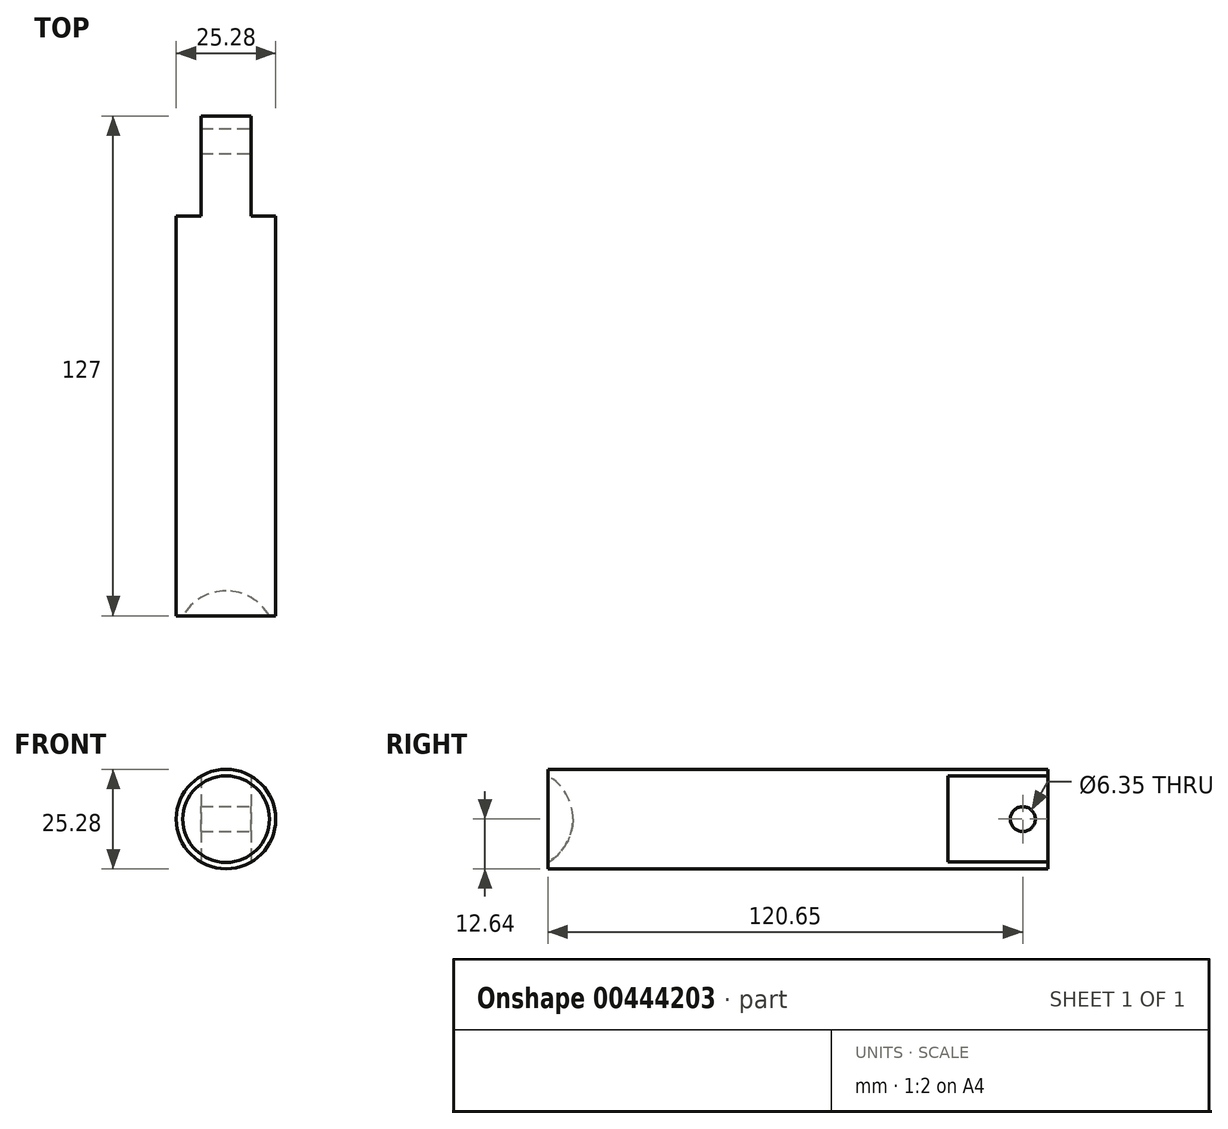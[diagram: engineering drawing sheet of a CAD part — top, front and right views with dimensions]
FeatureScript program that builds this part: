
annotation { "Feature Type Name" : "Feature", "Feature Type Description" : "" }
export const myFeature = defineFeature(function(context is Context, id is Id, definition is map)
    precondition{}
    {
        {
            var Q0;
            Q0=qCreatedBy(makeId("Right.planeOp"),FACE);
            var sketch = newSketch(context, id + "F0", { "sketchPlane" : qUnion([Q0])});
            skLineSegment(sketch, "E0.bottom", {"start": v(-63.5, 12.64) * mm, "end": v(63.5, 12.64) * mm});
            skLineSegment(sketch, "E0.left", {"start": v(-63.5, 12.64) * mm, "end": v(-63.5, 11) * mm});
            skLineSegment(sketch, "E0.right", {"start": v(63.5, 12.64) * mm, "end": v(63.5, 0) * mm});
            skArc(sketch, "E1", {"start": v(-57.15, 0) * mm, "mid": v(-58.85, 6.35) * mm, "end": v(-63.5, 11) * mm});
            skLineSegment(sketch, "E2", {"start": v(-57.15, 0) * mm, "end": v(63.5, 0) * mm});
            skPoint(sketch, "E3.orphan", {"position": v(63.5, -12.64) * mm});
            skLineSegment(sketch, "E4", {"start": v(-86.42, 0) * mm, "end": v(94.67, 0) * mm});
            skSolve(sketch);
        }
        {
            var Q0;
            Q0 = qSketchRegion(id + "F0", true);
            var Q1;
            Q1=sQuery(id+"F0.wireOp",EDGE,"E4");
            revolve(context, id + "F1", {"entities" : qUnion([Q0]), "axis" : qUnion([Q1]), "revolveType" : RevolveType.FULL});
        }
        {
            var Q0;
            Q0=makeQuery(id+"F1.opRevolve","SWEPT_FACE",FACE,{"disambiguationData":[OSD([sQuery(id+"F0.wireOp",EDGE,"E0.right")])]});
            var sketch = newSketch(context, id + "F2", { "sketchPlane" : qUnion([Q0])});
            skArc(sketch, "E5", {"start": v(6.35, -11) * mm, "mid": v(12.7, 0) * mm, "end": v(6.35, 11) * mm});
            skLineSegment(sketch, "E6", {"start": v(-6.35, 11) * mm, "end": v(-6.35, -11) * mm});
            skLineSegment(sketch, "E7", {"start": v(6.35, 11) * mm, "end": v(6.35, -11) * mm});
            skArc(sketch, "E8.trimOffspring", {"start": v(-6.35, 11) * mm, "mid": v(-12.7, 0) * mm, "end": v(-6.35, -11) * mm});
            skSolve(sketch);
        }
        {
            var Q0;
            Q0 = qSketchRegion(id + "F2", true);
            extrude(context, id + "F3", {"entities" : qUnion([Q0]), "operationType" : NewBodyOperationType.REMOVE, "oppositeDirection" : true, "depth" : 25.4 * mm});
        }
        {
            var Q0;
            Q0=makeQuery(id+"F3.boolean.opBoolean","COPY",FACE,{"derivedFrom":makeQuery(id+"F3.opExtrude","SWEPT_FACE",FACE,{"disambiguationData":[OSD([sQuery(id+"F2.wireOp",EDGE,"E6")])]})});
            var sketch = newSketch(context, id + "F4", { "sketchPlane" : qUnion([Q0])});
            skCircle(sketch, "E9", {"center": v(57.15, 0) * mm, "radius": 3.18 * mm});
            skPoint(sketch, "E9.centerSnap0", {"position": v(63.5, 0) * mm});
            skSolve(sketch);
        }
        {
            var Q0;
            Q0 = qSketchRegion(id + "F4", true);
            extrude(context, id + "F5", {"entities" : qUnion([Q0]), "operationType" : NewBodyOperationType.REMOVE, "oppositeDirection" : true, "depth" : 25.4 * mm});
        }
    });
